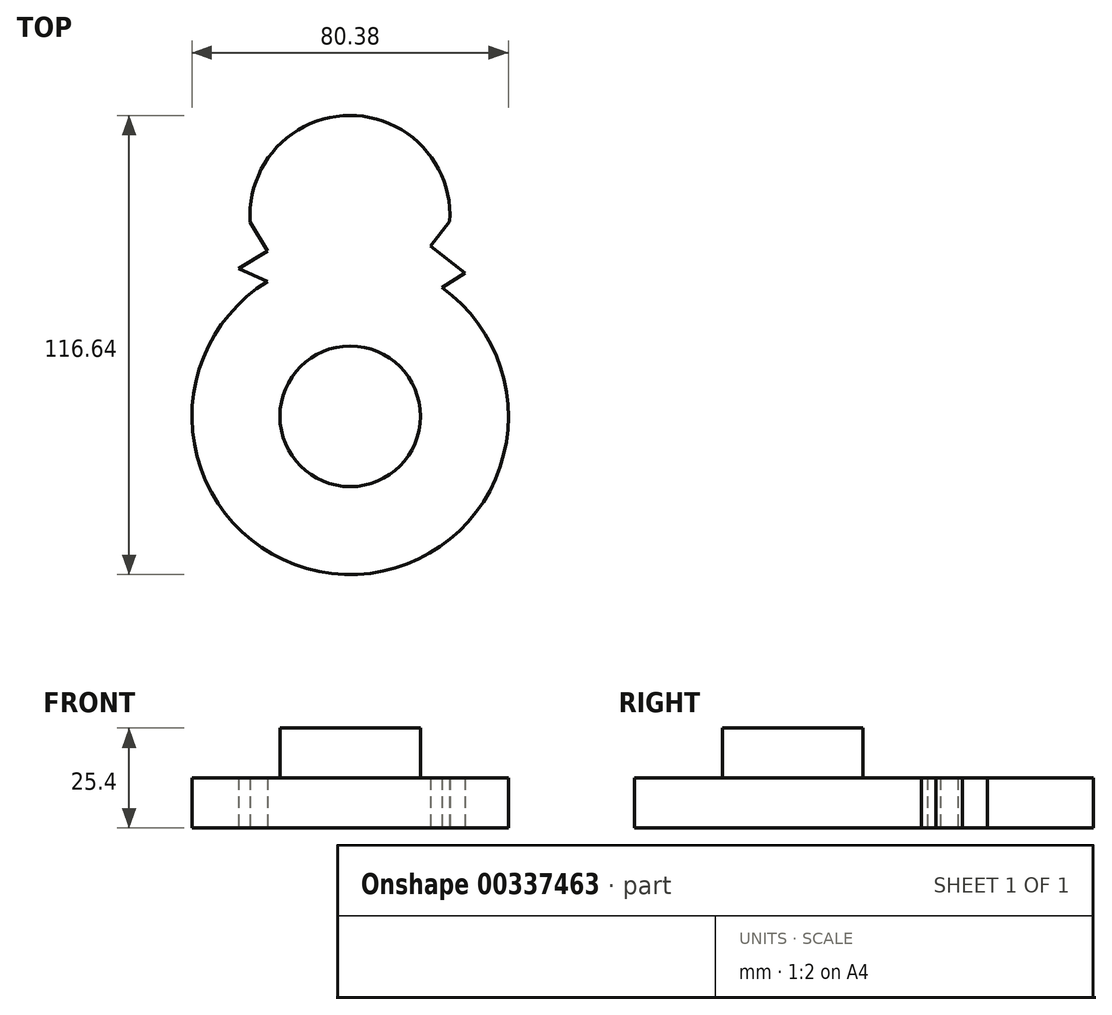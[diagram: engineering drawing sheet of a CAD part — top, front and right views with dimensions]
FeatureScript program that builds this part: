
annotation { "Feature Type Name" : "Feature", "Feature Type Description" : "" }
export const myFeature = defineFeature(function(context is Context, id is Id, definition is map)
    precondition{}
    {
        {
            var Q0;
            Q0=qCreatedBy(makeId("Top.planeOp"),FACE);
            var sketch = newSketch(context, id + "F0", { "sketchPlane" : qUnion([Q0])});
            skArc(sketch, "E0", {"start": v(-21, -25.56) * mm, "mid": v(-1.38, -99.99) * mm, "end": v(23.3, -27.08) * mm});
            skLineSegment(sketch, "E1", {"start": v(23.3, -27.08) * mm, "end": v(29.21, -23.4) * mm});
            skLineSegment(sketch, "E2", {"start": v(29.21, -23.4) * mm, "end": v(20.4, -16.6) * mm});
            skLineSegment(sketch, "E3", {"start": v(-21, -25.56) * mm, "end": v(-28.41, -22.2) * mm});
            skLineSegment(sketch, "E4", {"start": v(-28.41, -22.2) * mm, "end": v(-21, -17.8) * mm});
            skLineSegment(sketch, "E5", {"start": v(-21, -17.8) * mm, "end": v(-25.4, -10.4) * mm});
            skLineSegment(sketch, "E6", {"start": v(20.4, -16.6) * mm, "end": v(25.3, -10.27) * mm});
            skArc(sketch, "E7", {"start": v(25.3, -10.27) * mm, "mid": v(-0.12, 16.63) * mm, "end": v(-25.4, -10.4) * mm});
            skSolve(sketch);
        }
        {
            var Q0;
            Q0=makeQuery(id+"F0.imprint","IMPRINT",FACE,{"disambiguationData":[TD([[makeQuery(id+"F0.imprint","IMPRINT",EDGE,{"derivedFrom":sQuery(id+"F0.wireOp",EDGE,"E0")}),1.0]])]});
            extrude(context, id + "F1", {"entities" : qUnion([Q0]), "depth" : 12.7 * mm});
        }
        {
            var Q0;
            Q0=makeQuery(id+"F1.opExtrude","CAP_FACE",FACE,{"disambiguationData":[OSD([sQuery(id+"F0.wireOp",EDGE,"E0"),sQuery(id+"F0.wireOp",EDGE,"E1"),sQuery(id+"F0.wireOp",EDGE,"E2"),sQuery(id+"F0.wireOp",EDGE,"E3"),sQuery(id+"F0.wireOp",EDGE,"E4"),sQuery(id+"F0.wireOp",EDGE,"E5"),sQuery(id+"F0.wireOp",EDGE,"E6"),sQuery(id+"F0.wireOp",EDGE,"E7")])],"isStart":false});
            var sketch = newSketch(context, id + "F2", { "sketchPlane" : qUnion([Q0])});
            skArc(sketch, "E8", {"start": v(17.35, -43.69) * mm, "mid": v(1.22, -23.16) * mm, "end": v(-14.9, -43.69) * mm});
            skArc(sketch, "E9", {"start": v(-14.9, -43.69) * mm, "mid": v(-29.45, -52.77) * mm, "end": v(-21, -67.7) * mm});
            skArc(sketch, "E10", {"start": v(26.26, -66.48) * mm, "mid": v(30.54, -51.67) * mm, "end": v(17.35, -43.69) * mm});
            skPoint(sketch, "E10.startSnap0", {"position": v(26.26, -25.24) * mm});
            skCircle(sketch, "E11", {"center": v(0, -59.82) * mm, "radius": 17.85 * mm});
            skSolve(sketch);
        }
        {
            var Q0;
            Q0=makeQuery(id+"F2.imprint","IMPRINT",FACE,{"disambiguationData":[TD([[makeQuery(id+"F2.imprint","IMPRINT",EDGE,{"derivedFrom":sQuery(id+"F2.wireOp",EDGE,"E11")}),1.0]])]});
            extrude(context, id + "F3", {"entities" : qUnion([Q0]), "operationType" : NewBodyOperationType.ADD, "depth" : 12.7 * mm});
        }
    });
